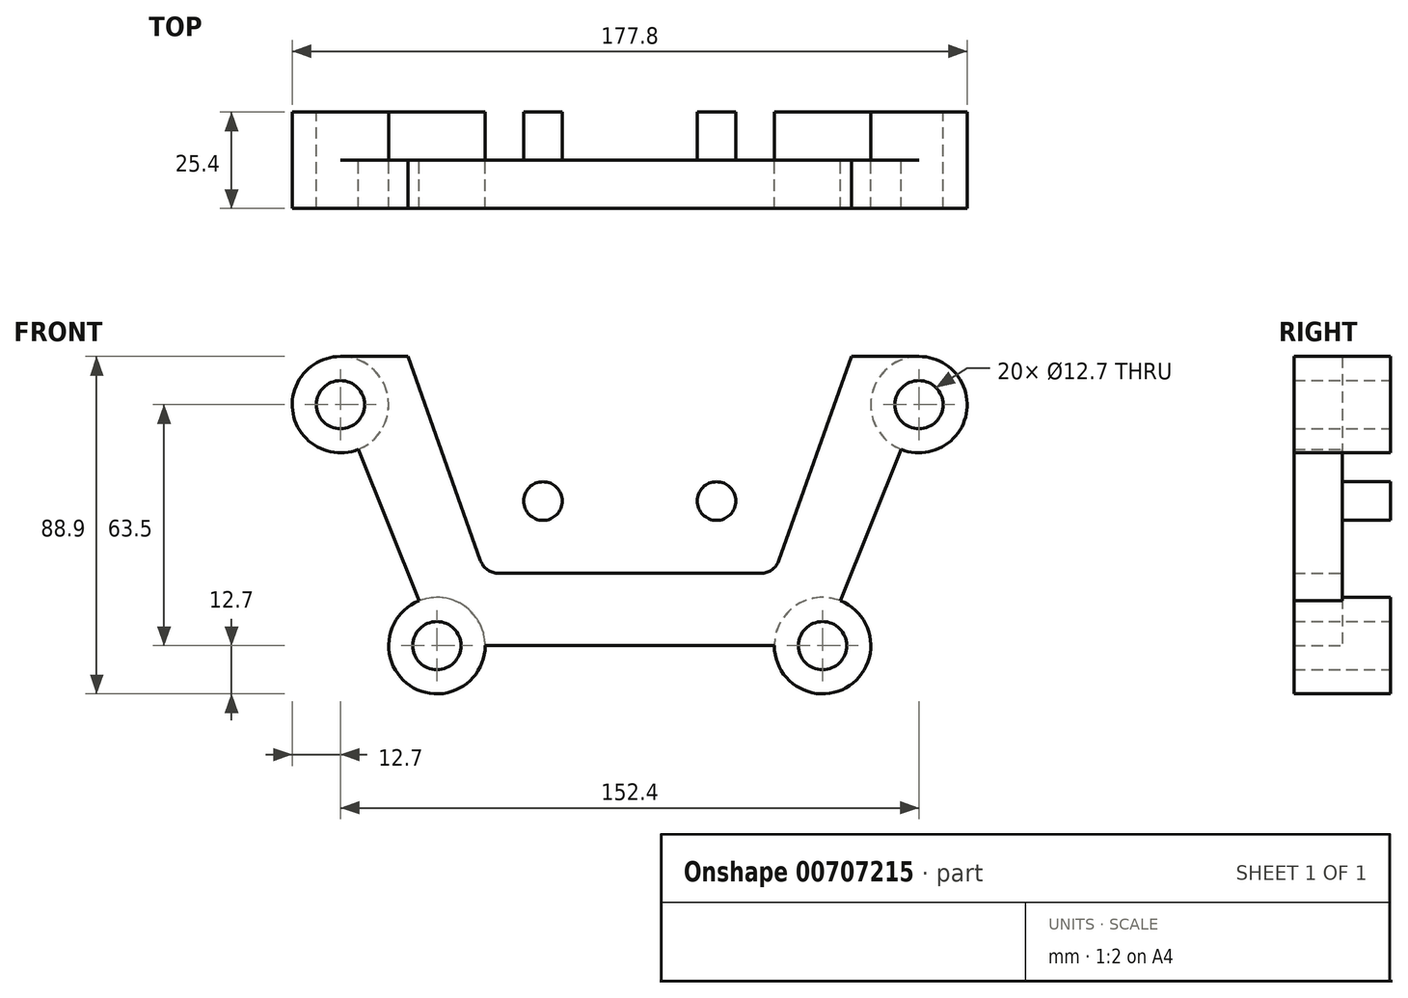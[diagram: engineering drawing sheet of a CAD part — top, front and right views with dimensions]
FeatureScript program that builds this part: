
annotation { "Feature Type Name" : "Feature", "Feature Type Description" : "" }
export const myFeature = defineFeature(function(context is Context, id is Id, definition is map)
    precondition{}
    {
        {
            var Q0;
            Q0=qCreatedBy(makeId("Front.planeOp"),FACE);
            var sketch = newSketch(context, id + "F0", { "sketchPlane" : qUnion([Q0])});
            skLineSegment(sketch, "E0", {"start": v(0, 0) * mm, "end": v(0, -38.1) * mm, "construction": true});
            skLineSegment(sketch, "E1", {"start": v(0, -38.1) * mm, "end": v(-50.8, -38.1) * mm});
            skLineSegment(sketch, "E2", {"start": v(0, -38.1) * mm, "end": v(50.8, -38.1) * mm});
            skLineSegment(sketch, "E3", {"start": v(0, 0) * mm, "end": v(0, 38.1) * mm, "construction": true});
            skLineSegment(sketch, "E4", {"start": v(0, 38.1) * mm, "end": v(-76.2, 38.1) * mm});
            skLineSegment(sketch, "E5", {"start": v(0, 38.1) * mm, "end": v(76.2, 38.1) * mm});
            skCircle(sketch, "E6", {"center": v(-76.2, 25.4) * mm, "radius": 12.7 * mm});
            skCircle(sketch, "E7", {"center": v(76.2, 25.4) * mm, "radius": 12.7 * mm});
            skCircle(sketch, "E8", {"center": v(-50.8, -38.1) * mm, "radius": 12.7 * mm});
            skCircle(sketch, "E9", {"center": v(50.8, -38.1) * mm, "radius": 12.7 * mm});
            skLineSegment(sketch, "E10", {"start": v(-76.2, 25.4) * mm, "end": v(-50.8, -38.1) * mm});
            skLineSegment(sketch, "E11", {"start": v(50.8, -38.1) * mm, "end": v(76.2, 25.4) * mm});
            skCircle(sketch, "E12", {"center": v(-76.2, 25.4) * mm, "radius": 6.35 * mm});
            skCircle(sketch, "E13", {"center": v(76.2, 25.4) * mm, "radius": 6.35 * mm});
            skCircle(sketch, "E14", {"center": v(50.8, -38.1) * mm, "radius": 6.35 * mm});
            skCircle(sketch, "E15", {"center": v(-50.8, -38.1) * mm, "radius": 6.35 * mm});
            skSolve(sketch);
        }
        {
            var Q0;
            {var subQ1=sQuery(id+"F0.wireOp",EDGE,"E4");Q0=makeQuery(id+"F0.imprint","IMPRINT",FACE,{"disambiguationData":[TD([[makeQuery(id+"F0.imprint","IMPRINT",EDGE,{"derivedFrom":subQ1}),1.0]])]});}
            var Q1;
            {var subQ0=sQuery(id+"F0.wireOp",EDGE,"E9");var subQ1=sQuery(id+"F0.wireOp",EDGE,"E2");var subQ2=makeQuery(id+"F0.imprint","INTERSECT",VERTEX,{"derivedFrom":[subQ1,subQ0]});Q1=makeQuery(id+"F0.imprint","IMPRINT",FACE,{"disambiguationData":[TD([[makeQuery(id+"F0.imprint","IMPRINT",EDGE,{"disambiguationData":[TD([[subQ2,-1.0]])],"derivedFrom":subQ1}),1.0]])]});}
            var Q2;
            {var subQ0=sQuery(id+"F0.wireOp",EDGE,"E8");var subQ1=sQuery(id+"F0.wireOp",EDGE,"E1");var subQ2=makeQuery(id+"F0.imprint","INTERSECT",VERTEX,{"derivedFrom":[subQ1,subQ0]});Q2=makeQuery(id+"F0.imprint","IMPRINT",FACE,{"disambiguationData":[TD([[makeQuery(id+"F0.imprint","IMPRINT",EDGE,{"disambiguationData":[TD([[subQ2,-1.0]])],"derivedFrom":subQ1}),-1.0]])]});}
            var Q3;
            Q3=makeQuery(id+"F0.imprint","IMPRINT",FACE,{"disambiguationData":[TD([[makeQuery(id+"F0.imprint","IMPRINT",EDGE,{"derivedFrom":sQuery(id+"F0.wireOp",EDGE,"E12")}),-1.0]])]});
            var Q4;
            Q4=makeQuery(id+"F0.imprint","IMPRINT",FACE,{"disambiguationData":[TD([[makeQuery(id+"F0.imprint","IMPRINT",EDGE,{"derivedFrom":sQuery(id+"F0.wireOp",EDGE,"E13")}),-1.0]])]});
            var Q5;
            {var subQ0=sQuery(id+"F0.wireOp",EDGE,"E8");var subQ1=sQuery(id+"F0.wireOp",EDGE,"E1");var subQ2=makeQuery(id+"F0.imprint","INTERSECT",VERTEX,{"derivedFrom":[subQ1,subQ0]});Q5=makeQuery(id+"F0.imprint","IMPRINT",FACE,{"disambiguationData":[TD([[makeQuery(id+"F0.imprint","IMPRINT",EDGE,{"disambiguationData":[TD([[subQ2,-1.0]])],"derivedFrom":subQ1}),1.0]])]});}
            var Q6;
            {var subQ0=sQuery(id+"F0.wireOp",EDGE,"E9");var subQ1=sQuery(id+"F0.wireOp",EDGE,"E2");var subQ2=makeQuery(id+"F0.imprint","INTERSECT",VERTEX,{"derivedFrom":[subQ1,subQ0]});Q6=makeQuery(id+"F0.imprint","IMPRINT",FACE,{"disambiguationData":[TD([[makeQuery(id+"F0.imprint","IMPRINT",EDGE,{"disambiguationData":[TD([[subQ2,-1.0]])],"derivedFrom":subQ1}),-1.0]])]});}
            extrude(context, id + "F1", {"entities" : qUnion([Q0, Q1, Q2, Q3, Q4, Q5, Q6]), "endBound" : BoundingType.SYMMETRIC, "depth" : 25.4 * mm, "offsetDistance" : 25.4 * mm});
        }
        {
            var Q0;
            Q0=qCreatedBy(makeId("Front.planeOp"),FACE);
            var sketch = newSketch(context, id + "F2", { "sketchPlane" : qUnion([Q0])});
            skLineSegment(sketch, "E16", {"start": v(0, -38.1) * mm, "end": v(0, 0) * mm, "construction": true});
            skPoint(sketch, "E17", {"position": v(0, -19.05) * mm});
            skLineSegment(sketch, "E18", {"start": v(0, -19.05) * mm, "end": v(-38.1, -19.05) * mm});
            skLineSegment(sketch, "E19", {"start": v(0, -19.05) * mm, "end": v(38.1, -19.05) * mm});
            skLineSegment(sketch, "E20", {"start": v(0, 0) * mm, "end": v(0, 38.1) * mm, "construction": true});
            skLineSegment(sketch, "E21", {"start": v(0, 38.1) * mm, "end": v(-58.42, 38.1) * mm});
            skLineSegment(sketch, "E22", {"start": v(0, 38.1) * mm, "end": v(58.42, 38.1) * mm});
            skLineSegment(sketch, "E23", {"start": v(-58.42, 38.1) * mm, "end": v(-38.1, -19.05) * mm});
            skLineSegment(sketch, "E24", {"start": v(38.1, -19.05) * mm, "end": v(58.42, 38.1) * mm});
            skSolve(sketch);
        }
        {
            var Q0;
            Q0 = qSketchRegion(id + "F2", true);
            extrude(context, id + "F3", {"entities" : qUnion([Q0]), "operationType" : NewBodyOperationType.REMOVE, "depth" : 38.1 * mm, "offsetDistance" : 25.4 * mm});
        }
        {
            var Q0;
            Q0=makeQuery(id+"F3.boolean.opBoolean","COPY",EDGE,{"derivedFrom":makeQuery(id+"F3.opExtrude","SWEPT_EDGE",EDGE,{"disambiguationData":[OSD([sQuery(id+"F2.wireOp",EDGE,"E18"),sQuery(id+"F2.wireOp",EDGE,"E23")])]})});
            var Q1;
            Q1=makeQuery(id+"F3.boolean.opBoolean","COPY",EDGE,{"derivedFrom":makeQuery(id+"F3.opExtrude","SWEPT_EDGE",EDGE,{"disambiguationData":[OSD([sQuery(id+"F2.wireOp",EDGE,"E19"),sQuery(id+"F2.wireOp",EDGE,"E24")])]})});
            fillet(context, id + "F4", {"entities" : qUnion([Q0, Q1]), "radius" : 5.08 * mm, "tangentPropagation" : true, "allowEdgeOverflow" : false});
        }
        {
            var Q0;
            {var subQ1=sQuery(id+"F0.wireOp",EDGE,"E4");Q0=makeQuery(id+"F0.imprint","IMPRINT",FACE,{"disambiguationData":[TD([[makeQuery(id+"F0.imprint","IMPRINT",EDGE,{"derivedFrom":subQ1}),1.0]])]});}
            var sketch = newSketch(context, id + "F5", { "sketchPlane" : qUnion([Q0])});
            skLineSegment(sketch, "E25", {"start": v(0, 0) * mm, "end": v(-22.86, 0) * mm, "construction": true});
            skLineSegment(sketch, "E26", {"start": v(0, 0) * mm, "end": v(22.86, 0) * mm, "construction": true});
            skCircle(sketch, "E27", {"center": v(-22.86, 0) * mm, "radius": 5.08 * mm});
            skCircle(sketch, "E28", {"center": v(22.86, 0) * mm, "radius": 5.08 * mm});
            skSolve(sketch);
        }
        {
            var Q0;
            Q0=makeQuery(id+"F5.imprint","IMPRINT",FACE,{"disambiguationData":[TD([[makeQuery(id+"F5.imprint","IMPRINT",EDGE,{"derivedFrom":sQuery(id+"F5.wireOp",EDGE,"E27")}),-1.0]])]});
            var Q1;
            Q1=sQuery(id+"F5.wireOp",EDGE,"E27");
            var Q2;
            Q2=sQuery(id+"F5.wireOp",EDGE,"E28");
            extrude(context, id + "F6", {"entities" : qUnion([Q0]), "operationType" : NewBodyOperationType.REMOVE, "surfaceEntities" : qUnion([Q1, Q2]), "oppositeDirection" : true, "depth" : 25.4 * mm, "offsetDistance" : 25.4 * mm});
        }
    });
